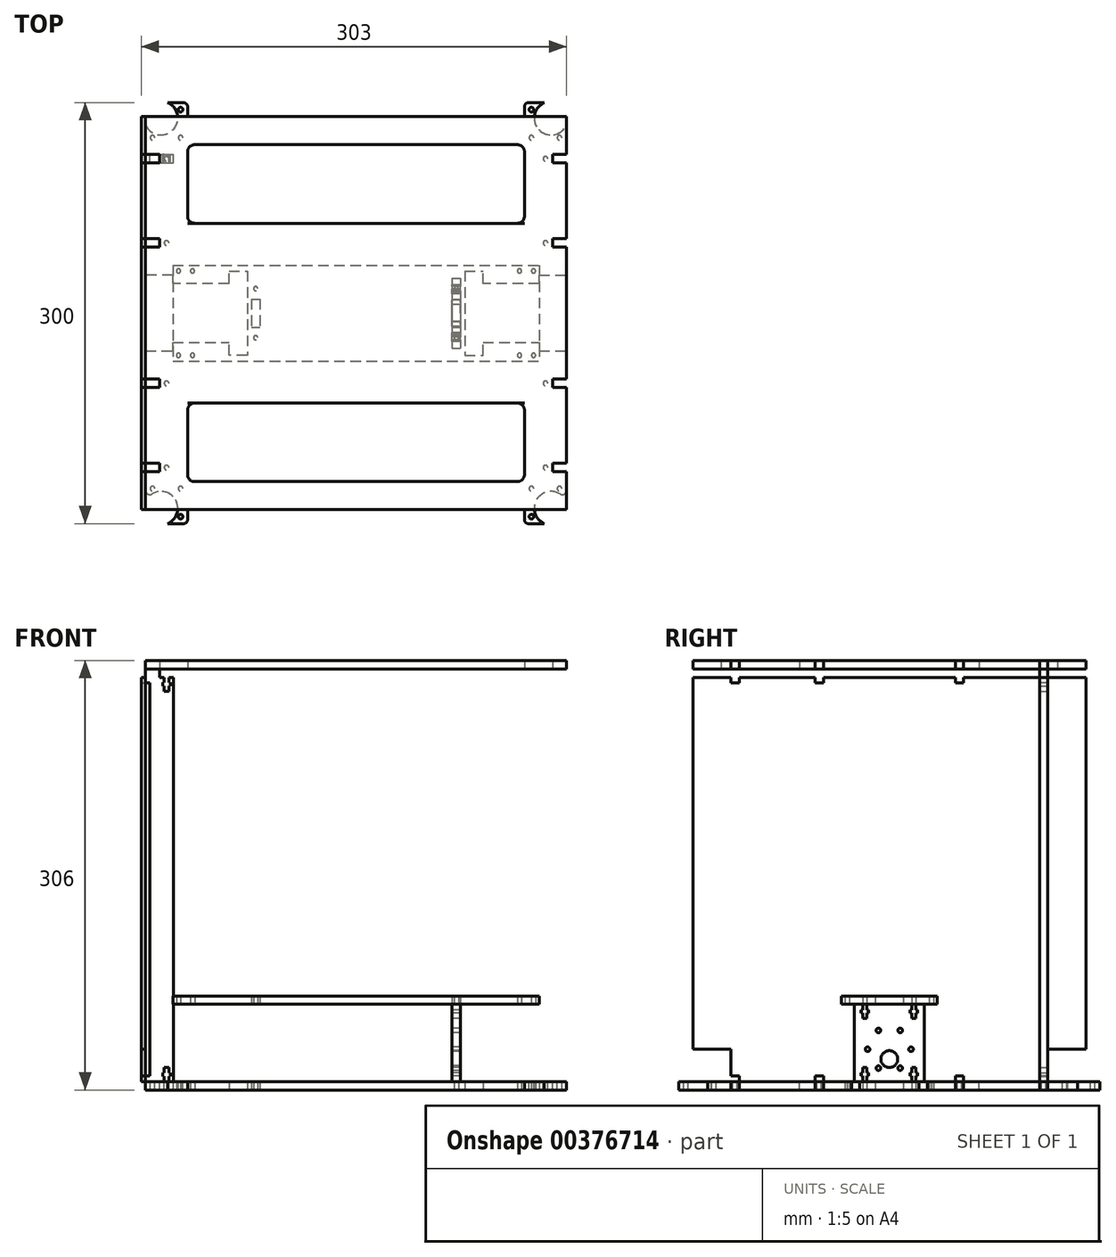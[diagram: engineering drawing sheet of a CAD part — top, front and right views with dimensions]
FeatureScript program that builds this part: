
annotation { "Feature Type Name" : "Feature", "Feature Type Description" : "" }
export const myFeature = defineFeature(function(context is Context, id is Id, definition is map)
    precondition{}
    {
        {
            var Q0;
            Q0=qCreatedBy(makeId("Top.planeOp"),FACE);
            var sketch = newSketch(context, id + "F0", { "sketchPlane" : qUnion([Q0])});
            skLineSegment(sketch, "E0.bottom", {"start": v(150, 34.05) * mm, "end": v(-150, 34.05) * mm});
            skLineSegment(sketch, "E0.top", {"start": v(150, -34.05) * mm, "end": v(-150, -34.05) * mm});
            skLineSegment(sketch, "E0.left", {"start": v(150, 34.05) * mm, "end": v(150, 27) * mm});
            skLineSegment(sketch, "E0.right", {"start": v(-150, 34.05) * mm, "end": v(-150, 27) * mm});
            skPoint(sketch, "E0.middle", {"position": v(0, 0) * mm});
            skPoint(sketch, "E1", {"position": v(126.5, -30.05) * mm});
            skPoint(sketch, "E2", {"position": v(116.5, -30.05) * mm});
            skPoint(sketch, "E3", {"position": v(126.5, 30.05) * mm});
            skPoint(sketch, "E4", {"position": v(116.5, 30.05) * mm});
            skPoint(sketch, "E5", {"position": v(-116.5, -30.05) * mm});
            skPoint(sketch, "E6", {"position": v(-126.5, -30.05) * mm});
            skPoint(sketch, "E7", {"position": v(-126.5, 30.05) * mm});
            skPoint(sketch, "E8", {"position": v(-116.5, 30.05) * mm});
            skLineSegment(sketch, "E9", {"start": v(130.5, 21) * mm, "end": v(90.5, 21) * mm});
            skLineSegment(sketch, "E10", {"start": v(90.5, 21) * mm, "end": v(90.5, -21) * mm, "construction": true});
            skLineSegment(sketch, "E11", {"start": v(90.5, -21) * mm, "end": v(130.5, -21) * mm});
            skLineSegment(sketch, "E12", {"start": v(130.5, -21) * mm, "end": v(130.5, -27) * mm});
            skLineSegment(sketch, "E13", {"start": v(130.5, -27) * mm, "end": v(150, -27) * mm});
            skLineSegment(sketch, "E14", {"start": v(130.5, 21) * mm, "end": v(130.5, 27) * mm});
            skLineSegment(sketch, "E15", {"start": v(130.5, 27) * mm, "end": v(150, 27) * mm});
            skLineSegment(sketch, "E16.trimOffspring", {"start": v(150, -27) * mm, "end": v(150, -34.05) * mm});
            skPoint(sketch, "E17", {"position": v(90.5, 0) * mm});
            skLineSegment(sketch, "E18", {"start": v(-150, -27) * mm, "end": v(-130.5, -27) * mm});
            skLineSegment(sketch, "E19", {"start": v(-130.5, -27) * mm, "end": v(-130.5, -21) * mm});
            skLineSegment(sketch, "E20", {"start": v(-130.5, -21) * mm, "end": v(-90.5, -21) * mm});
            skLineSegment(sketch, "E21", {"start": v(-90.5, 21) * mm, "end": v(-130.5, 21) * mm});
            skLineSegment(sketch, "E22", {"start": v(-130.5, 21) * mm, "end": v(-130.5, 27) * mm});
            skLineSegment(sketch, "E23", {"start": v(-130.5, 27) * mm, "end": v(-150, 27) * mm});
            skLineSegment(sketch, "E24.trimOffspring", {"start": v(-150, -27) * mm, "end": v(-150, -34.05) * mm});
            skLineSegment(sketch, "E25", {"start": v(68.5, 25) * mm, "end": v(68.5, -25) * mm, "construction": true});
            skPoint(sketch, "E26", {"position": v(68.5, 0) * mm});
            skLineSegment(sketch, "E27.bottom", {"start": v(74.5, 10) * mm, "end": v(68.5, 10) * mm});
            skLineSegment(sketch, "E27.top", {"start": v(74.5, -10) * mm, "end": v(68.5, -10) * mm});
            skLineSegment(sketch, "E27.left", {"start": v(74.5, 10) * mm, "end": v(74.5, -10) * mm});
            skLineSegment(sketch, "E27.right", {"start": v(68.5, 10) * mm, "end": v(68.5, -10) * mm});
            skCircle(sketch, "E28", {"center": v(71.5, 17.5) * mm, "radius": 1.5 * mm});
            skCircle(sketch, "E29", {"center": v(71.5, -17.5) * mm, "radius": 1.5 * mm});
            skLineSegment(sketch, "E30", {"start": v(71.5, 17.5) * mm, "end": v(71.5, -17.5) * mm, "construction": true});
            skPoint(sketch, "E31", {"position": v(71.5, 0) * mm});
            skLineSegment(sketch, "E32", {"start": v(68.5, 0) * mm, "end": v(74.5, 0) * mm, "construction": true});
            skLineSegment(sketch, "E33.bottom", {"start": v(-74.5, 10) * mm, "end": v(-68.5, 10) * mm});
            skLineSegment(sketch, "E33.top", {"start": v(-74.5, -10) * mm, "end": v(-68.5, -10) * mm});
            skLineSegment(sketch, "E33.left", {"start": v(-74.5, 10) * mm, "end": v(-74.5, -10) * mm});
            skLineSegment(sketch, "E33.right", {"start": v(-68.5, 10) * mm, "end": v(-68.5, -10) * mm});
            skCircle(sketch, "E34", {"center": v(-71.5, 17.5) * mm, "radius": 1.5 * mm});
            skCircle(sketch, "E35", {"center": v(-71.5, -17.5) * mm, "radius": 1.5 * mm});
            skLineSegment(sketch, "E36.bottom", {"start": v(77.5, 30) * mm, "end": v(90.5, 30) * mm});
            skLineSegment(sketch, "E36.top", {"start": v(77.5, -30) * mm, "end": v(90.5, -30) * mm});
            skLineSegment(sketch, "E36.left", {"start": v(77.5, 30) * mm, "end": v(77.5, -30) * mm});
            skLineSegment(sketch, "E37", {"start": v(90.5, -30) * mm, "end": v(90.5, -21) * mm});
            skLineSegment(sketch, "E38", {"start": v(90.5, 21) * mm, "end": v(90.5, 30) * mm});
            skLineSegment(sketch, "E39", {"start": v(-90.5, 21) * mm, "end": v(-90.5, 30) * mm});
            skLineSegment(sketch, "E40", {"start": v(-90.5, 30) * mm, "end": v(-77.5, 30) * mm});
            skLineSegment(sketch, "E41", {"start": v(-77.5, 30) * mm, "end": v(-77.5, -30) * mm});
            skLineSegment(sketch, "E42", {"start": v(-77.5, -30) * mm, "end": v(-90.5, -30) * mm});
            skLineSegment(sketch, "E43", {"start": v(-90.5, -30) * mm, "end": v(-90.5, -21) * mm});
            skSolve(sketch);
        }
        {
            var Q0;
            Q0=qSketchRegion(id+"F0",true);
            extrude(context, id + "F1", {"entities" : qUnion([Q0]), "depth" : 6 * mm});
        }
        {
            var Q0;
            Q0=sQuery(id+"F0.wireOp",VERTEX,"E1");
            var Q1;
            Q1=sQuery(id+"F0.wireOp",VERTEX,"E2");
            var Q2;
            Q2=sQuery(id+"F0.wireOp",VERTEX,"E3");
            var Q3;
            Q3=sQuery(id+"F0.wireOp",VERTEX,"E4");
            var Q4;
            Q4=sQuery(id+"F0.wireOp",VERTEX,"E5");
            var Q5;
            Q5=sQuery(id+"F0.wireOp",VERTEX,"E6");
            var Q6;
            Q6=sQuery(id+"F0.wireOp",VERTEX,"E8");
            var Q7;
            Q7=sQuery(id+"F0.wireOp",VERTEX,"E7");
            var Q8;
            Q8=makeQuery(id+"F1.opExtrude","SWEPT_BODY",BODY,{"disambiguationData":[OSD([sQuery(id+"F0.wireOp",EDGE,"E0.bottom"),sQuery(id+"F0.wireOp",EDGE,"E0.top"),sQuery(id+"F0.wireOp",EDGE,"E0.left"),sQuery(id+"F0.wireOp",EDGE,"E0.right")])]});
            hole(context, id + "F2", {"style" : HoleStyle.SIMPLE, "endStyle" : HoleEndStyle.THROUGH, "oppositeDirection" : true, "standardTappedOrClearance" : lookupTablePath({ "standard" : "ISO", "size" : "3", "type" : "Drilled" }), "standardBlindInLast" : lookupTablePath({ "standard" : "ISO", "size" : "3", "type" : "Drilled" }), "holeDiameter" : 3 * mm, "tappedDepth" : 10.9 * mm, "tapClearance" : 3, "locations" : qUnion([Q0, Q1, Q2, Q3, Q4, Q5, Q6, Q7]), "scope" : qUnion([Q8])});
        }
        {
            var Q0;
            Q0=makeQuery(id+"F1.opExtrude","CAP_FACE",FACE,{"disambiguationData":[OSD([sQuery(id+"F0.wireOp",EDGE,"E0.bottom"),sQuery(id+"F0.wireOp",EDGE,"E0.top"),sQuery(id+"F0.wireOp",EDGE,"E0.left"),sQuery(id+"F0.wireOp",EDGE,"E0.right"),sQuery(id+"F0.wireOp",EDGE,"E9"),sQuery(id+"F0.wireOp",EDGE,"E10"),sQuery(id+"F0.wireOp",EDGE,"E11"),sQuery(id+"F0.wireOp",EDGE,"E12"),sQuery(id+"F0.wireOp",EDGE,"E13"),sQuery(id+"F0.wireOp",EDGE,"E14"),sQuery(id+"F0.wireOp",EDGE,"E15"),sQuery(id+"F0.wireOp",EDGE,"E16.trimOffspring"),sQuery(id+"F0.wireOp",EDGE,"E18"),sQuery(id+"F0.wireOp",EDGE,"E19"),sQuery(id+"F0.wireOp",EDGE,"E20"),sQuery(id+"F0.wireOp",EDGE,"jEcUEht7-0Wzt-mQMa-QwQx-0Txn2W36VDiV"),sQuery(id+"F0.wireOp",EDGE,"E21"),sQuery(id+"F0.wireOp",EDGE,"E22"),sQuery(id+"F0.wireOp",EDGE,"E23"),sQuery(id+"F0.wireOp",EDGE,"E24.trimOffspring")])],"isStart":false});
            var sketch = newSketch(context, id + "F3", { "sketchPlane" : qUnion([Q0])});
            skLineSegment(sketch, "E44.bottom", {"start": v(68.5, 25) * mm, "end": v(74.5, 25) * mm});
            skLineSegment(sketch, "E44.top", {"start": v(68.5, -25) * mm, "end": v(74.5, -25) * mm});
            skLineSegment(sketch, "E44.left", {"start": v(68.5, 25) * mm, "end": v(68.5, -25) * mm});
            skLineSegment(sketch, "E44.right", {"start": v(74.5, 25) * mm, "end": v(74.5, -25) * mm});
            skSolve(sketch);
        }
        {
            var Q0;
            Q0=qSketchRegion(id+"F3",true);
            extrude(context, id + "F4", {"entities" : qUnion([Q0]), "depth" : 55 * mm});
        }
        {
            var Q0;
            Q0=makeQuery(id+"F4.opExtrude","CAP_FACE",FACE,{"disambiguationData":[OSD([sQuery(id+"F3.wireOp",EDGE,"E44.bottom"),sQuery(id+"F3.wireOp",EDGE,"E44.top"),sQuery(id+"F3.wireOp",EDGE,"E44.left"),sQuery(id+"F3.wireOp",EDGE,"E44.right")])],"isStart":true});
            var sketch = newSketch(context, id + "F5", { "sketchPlane" : qUnion([Q0])});
            skLineSegment(sketch, "E45.bottom", {"start": v(74.5, -10) * mm, "end": v(68.5, -10) * mm});
            skLineSegment(sketch, "E45.top", {"start": v(74.5, 10) * mm, "end": v(68.5, 10) * mm});
            skLineSegment(sketch, "E45.left", {"start": v(74.5, -10) * mm, "end": v(74.5, 10) * mm});
            skLineSegment(sketch, "E45.right", {"start": v(68.5, -10) * mm, "end": v(68.5, 10) * mm});
            skSolve(sketch);
        }
        {
            var Q0;
            Q0=qSketchRegion(id+"F5",true);
            extrude(context, id + "F6", {"entities" : qUnion([Q0]), "operationType" : NewBodyOperationType.ADD, "depth" : 6 * mm});
        }
        {
            var Q0;
            Q0=makeQuery(id+"F4.opExtrude","SWEPT_FACE",FACE,{"disambiguationData":[OSD([sQuery(id+"F3.wireOp",EDGE,"E44.left")])]});
            var sketch = newSketch(context, id + "F7", { "sketchPlane" : qUnion([Q0])});
            skCircle(sketch, "E46", {"center": v(0, 29) * mm, "radius": 15.5 * mm, "construction": true});
            skCircle(sketch, "E47", {"center": v(0, 22) * mm, "radius": 6 * mm});
            skCircle(sketch, "E48", {"center": v(7.75, 15.58) * mm, "radius": 1.65 * mm});
            skCircle(sketch, "E49", {"center": v(15.5, 29) * mm, "radius": 1.65 * mm});
            skCircle(sketch, "E50", {"center": v(7.75, 42.42) * mm, "radius": 1.65 * mm});
            skCircle(sketch, "E51", {"center": v(-7.75, 42.42) * mm, "radius": 1.65 * mm});
            skCircle(sketch, "E52", {"center": v(-15.5, 29) * mm, "radius": 1.65 * mm});
            skCircle(sketch, "E53", {"center": v(-7.75, 15.58) * mm, "radius": 1.65 * mm});
            skLineSegment(sketch, "E54", {"start": v(-7.75, 15.58) * mm, "end": v(0, 29) * mm, "construction": true});
            skLineSegment(sketch, "E55", {"start": v(7.75, 15.58) * mm, "end": v(0, 29) * mm, "construction": true});
            skLineSegment(sketch, "E56", {"start": v(0, 29) * mm, "end": v(15.5, 29) * mm, "construction": true});
            skLineSegment(sketch, "E57", {"start": v(0, 29) * mm, "end": v(7.75, 42.42) * mm, "construction": true});
            skLineSegment(sketch, "E58", {"start": v(0, 29) * mm, "end": v(-7.75, 42.42) * mm, "construction": true});
            skLineSegment(sketch, "E59", {"start": v(0, 29) * mm, "end": v(-15.5, 29) * mm, "construction": true});
            skSolve(sketch);
        }
        {
            var Q0;
            Q0=qSketchRegion(id+"F7",true);
            extrude(context, id + "F8", {"entities" : qUnion([Q0]), "operationType" : NewBodyOperationType.REMOVE, "endBound" : BoundingType.UP_TO_NEXT, "oppositeDirection" : true, "depth" : 25 * mm});
        }
        {
            var Q0;
            Q0=makeQuery(id+"F6.boolean.opBoolean","MERGE",FACE,{"derivedFrom":[makeQuery(id+"F4.opExtrude","SWEPT_FACE",FACE,{"disambiguationData":[OSD([sQuery(id+"F3.wireOp",EDGE,"E44.left")])]}),makeQuery(id+"F6.opExtrude","SWEPT_FACE",FACE,{"disambiguationData":[OSD([sQuery(id+"F5.wireOp",EDGE,"E45.right")])]})]});
            var sketch = newSketch(context, id + "F9", { "sketchPlane" : qUnion([Q0])});
            skLineSegment(sketch, "E60", {"start": v(19, 6) * mm, "end": v(19, 10) * mm});
            skLineSegment(sketch, "E61", {"start": v(19, 10) * mm, "end": v(20.2, 10) * mm});
            skLineSegment(sketch, "E62", {"start": v(20.2, 10) * mm, "end": v(20.2, 12.3) * mm});
            skLineSegment(sketch, "E63", {"start": v(20.2, 12.3) * mm, "end": v(19, 12.3) * mm});
            skLineSegment(sketch, "E64", {"start": v(19, 12.3) * mm, "end": v(19, 16) * mm});
            skLineSegment(sketch, "E65", {"start": v(19, 16) * mm, "end": v(16, 16) * mm});
            skLineSegment(sketch, "E66", {"start": v(16, 16) * mm, "end": v(16, 12.3) * mm});
            skLineSegment(sketch, "E67", {"start": v(16, 12.3) * mm, "end": v(14.8, 12.3) * mm});
            skLineSegment(sketch, "E68", {"start": v(14.8, 12.3) * mm, "end": v(14.8, 10) * mm});
            skLineSegment(sketch, "E69", {"start": v(14.8, 10) * mm, "end": v(16, 10) * mm});
            skLineSegment(sketch, "E70", {"start": v(16, 10) * mm, "end": v(16, 6) * mm});
            skLineSegment(sketch, "E71", {"start": v(16, 6) * mm, "end": v(19, 6) * mm});
            skPoint(sketch, "E72", {"position": v(17.5, 16) * mm});
            skLineSegment(sketch, "E73", {"start": v(-19, 6) * mm, "end": v(-19, 10) * mm});
            skLineSegment(sketch, "E74", {"start": v(-19, 10) * mm, "end": v(-20.2, 10) * mm});
            skLineSegment(sketch, "E75", {"start": v(-20.2, 10) * mm, "end": v(-20.2, 12.3) * mm});
            skLineSegment(sketch, "E76", {"start": v(-20.2, 12.3) * mm, "end": v(-19, 12.3) * mm});
            skLineSegment(sketch, "E77", {"start": v(-19, 12.3) * mm, "end": v(-19, 16) * mm});
            skLineSegment(sketch, "E78", {"start": v(-19, 16) * mm, "end": v(-16, 16) * mm});
            skLineSegment(sketch, "E79", {"start": v(-16, 16) * mm, "end": v(-16, 12.3) * mm});
            skLineSegment(sketch, "E80", {"start": v(-16, 12.3) * mm, "end": v(-14.8, 12.3) * mm});
            skLineSegment(sketch, "E81", {"start": v(-14.8, 12.3) * mm, "end": v(-14.8, 10) * mm});
            skLineSegment(sketch, "E82", {"start": v(-14.8, 10) * mm, "end": v(-16, 10) * mm});
            skLineSegment(sketch, "E83", {"start": v(-16, 10) * mm, "end": v(-16, 6) * mm});
            skLineSegment(sketch, "E84", {"start": v(-16, 6) * mm, "end": v(-19, 6) * mm});
            skLineSegment(sketch, "E85", {"start": v(25, 33.5) * mm, "end": v(-25, 33.5) * mm, "construction": true});
            skLineSegment(sketch, "E86", {"start": v(16, 61) * mm, "end": v(19, 61) * mm});
            skLineSegment(sketch, "E87", {"start": v(19, 61) * mm, "end": v(19, 57) * mm});
            skLineSegment(sketch, "E88", {"start": v(19, 57) * mm, "end": v(20.2, 57) * mm});
            skLineSegment(sketch, "E89", {"start": v(20.2, 57) * mm, "end": v(20.2, 54.7) * mm});
            skLineSegment(sketch, "E90", {"start": v(20.2, 54.7) * mm, "end": v(19, 54.7) * mm});
            skLineSegment(sketch, "E91", {"start": v(19, 54.7) * mm, "end": v(19, 51) * mm});
            skLineSegment(sketch, "E92", {"start": v(19, 51) * mm, "end": v(16, 51) * mm});
            skLineSegment(sketch, "E93", {"start": v(16, 51) * mm, "end": v(16, 54.7) * mm});
            skLineSegment(sketch, "E94", {"start": v(16, 54.7) * mm, "end": v(14.8, 54.7) * mm});
            skLineSegment(sketch, "E95", {"start": v(14.8, 54.7) * mm, "end": v(14.8, 57) * mm});
            skLineSegment(sketch, "E96", {"start": v(14.8, 57) * mm, "end": v(16, 57) * mm});
            skLineSegment(sketch, "E97", {"start": v(16, 57) * mm, "end": v(16, 61) * mm});
            skLineSegment(sketch, "E98", {"start": v(-19, 61) * mm, "end": v(-16, 61) * mm});
            skLineSegment(sketch, "E99", {"start": v(-16, 61) * mm, "end": v(-16, 57) * mm});
            skLineSegment(sketch, "E100", {"start": v(-16, 57) * mm, "end": v(-14.8, 57) * mm});
            skLineSegment(sketch, "E101", {"start": v(-14.8, 57) * mm, "end": v(-14.8, 54.7) * mm});
            skLineSegment(sketch, "E102", {"start": v(-14.8, 54.7) * mm, "end": v(-16, 54.7) * mm});
            skLineSegment(sketch, "E103", {"start": v(-16, 54.7) * mm, "end": v(-16, 51) * mm});
            skLineSegment(sketch, "E104", {"start": v(-16, 51) * mm, "end": v(-19, 51) * mm});
            skLineSegment(sketch, "E105", {"start": v(-19, 51) * mm, "end": v(-19, 54.7) * mm});
            skLineSegment(sketch, "E106", {"start": v(-19, 54.7) * mm, "end": v(-20.2, 54.7) * mm});
            skLineSegment(sketch, "E107", {"start": v(-20.2, 54.7) * mm, "end": v(-20.2, 57) * mm});
            skLineSegment(sketch, "E108", {"start": v(-20.2, 57) * mm, "end": v(-19, 57) * mm});
            skLineSegment(sketch, "E109", {"start": v(-19, 57) * mm, "end": v(-19, 61) * mm});
            skSolve(sketch);
        }
        {
            var Q0;
            Q0=qSketchRegion(id+"F9",true);
            extrude(context, id + "F10", {"entities" : qUnion([Q0]), "operationType" : NewBodyOperationType.REMOVE, "endBound" : BoundingType.UP_TO_NEXT, "oppositeDirection" : true, "depth" : 25 * mm});
        }
        {
            var Q0;
            {var subQ0=sQuery(id+"F3.wireOp",EDGE,"E44.right");var subQ1=sQuery(id+"F3.wireOp",EDGE,"E44.left");Q0=makeQuery(id+"F10.boolean.opBoolean","SPLIT",FACE,{"disambiguationData":[TD([makeQuery(id+"F10.opExtrude","SWEPT_FACE",FACE,{"disambiguationData":[OSD([sQuery(id+"F9.wireOp",EDGE,"E97")])]})])],"derivedFrom":makeQuery(id+"F4.opExtrude","CAP_FACE",FACE,{"disambiguationData":[OSD([sQuery(id+"F3.wireOp",EDGE,"E44.bottom"),sQuery(id+"F3.wireOp",EDGE,"E44.top"),subQ1,subQ0])],"isStart":false})});}
            var sketch = newSketch(context, id + "F11", { "sketchPlane" : qUnion([Q0])});
            skLineSegment(sketch, "E110.bottom", {"start": v(68.5, 10) * mm, "end": v(74.5, 10) * mm});
            skLineSegment(sketch, "E110.top", {"start": v(68.5, -10) * mm, "end": v(74.5, -10) * mm});
            skLineSegment(sketch, "E110.left", {"start": v(68.5, 10) * mm, "end": v(68.5, -10) * mm});
            skLineSegment(sketch, "E110.right", {"start": v(74.5, 10) * mm, "end": v(74.5, -10) * mm});
            skSolve(sketch);
        }
        {
            var Q0;
            Q0=qSketchRegion(id+"F11",true);
            extrude(context, id + "F12", {"entities" : qUnion([Q0]), "operationType" : NewBodyOperationType.ADD, "depth" : 6 * mm});
        }
        {
            var Q0;
            {var subQ2=sQuery(id+"F3.wireOp",EDGE,"E44.right");var subQ4=sQuery(id+"F3.wireOp",EDGE,"E44.left");var subQ6=makeQuery(id+"F10.opExtrude","SWEPT_FACE",FACE,{"disambiguationData":[OSD([sQuery(id+"F9.wireOp",EDGE,"E99")])]});Q0=makeQuery(id+"F12.boolean.opBoolean","SPLIT",FACE,{"disambiguationData":[TD([makeQuery(id+"F10.boolean.opBoolean","COPY",FACE,{"derivedFrom":subQ6})])],"derivedFrom":makeQuery(id+"F10.boolean.opBoolean","SPLIT",FACE,{"disambiguationData":[TD([makeQuery(id+"F10.opExtrude","SWEPT_FACE",FACE,{"disambiguationData":[OSD([sQuery(id+"F9.wireOp",EDGE,"E97")])]})])],"derivedFrom":makeQuery(id+"F4.opExtrude","CAP_FACE",FACE,{"disambiguationData":[OSD([sQuery(id+"F3.wireOp",EDGE,"E44.bottom"),sQuery(id+"F3.wireOp",EDGE,"E44.top"),subQ4,subQ2])],"isStart":false})})});}
            var sketch = newSketch(context, id + "F13", { "sketchPlane" : qUnion([Q0])});
            skLineSegment(sketch, "E111.bottom", {"start": v(-130.5, 34.05) * mm, "end": v(130.5, 34.05) * mm});
            skLineSegment(sketch, "E111.top", {"start": v(-130.5, -34.05) * mm, "end": v(130.5, -34.05) * mm});
            skLineSegment(sketch, "E111.left", {"start": v(-130.5, 34.05) * mm, "end": v(-130.5, -34.05) * mm});
            skLineSegment(sketch, "E111.right", {"start": v(130.5, 34.05) * mm, "end": v(130.5, -34.05) * mm});
            skLineSegment(sketch, "E112.bottom", {"start": v(68.5, 10) * mm, "end": v(74.5, 10) * mm});
            skLineSegment(sketch, "E112.top", {"start": v(68.5, -10) * mm, "end": v(74.5, -10) * mm});
            skLineSegment(sketch, "E112.left", {"start": v(68.5, 10) * mm, "end": v(68.5, -10) * mm});
            skLineSegment(sketch, "E112.right", {"start": v(74.5, 10) * mm, "end": v(74.5, -10) * mm});
            skLineSegment(sketch, "E113", {"start": v(0, 34.05) * mm, "end": v(0, -34.05) * mm, "construction": true});
            skLineSegment(sketch, "E114.bottom", {"start": v(-74.5, 10) * mm, "end": v(-68.5, 10) * mm});
            skLineSegment(sketch, "E114.top", {"start": v(-74.5, -10) * mm, "end": v(-68.5, -10) * mm});
            skLineSegment(sketch, "E114.left", {"start": v(-74.5, 10) * mm, "end": v(-74.5, -10) * mm});
            skLineSegment(sketch, "E114.right", {"start": v(-68.5, 10) * mm, "end": v(-68.5, -10) * mm});
            skCircle(sketch, "E115", {"center": v(-71.5, 17.5) * mm, "radius": 1.5 * mm});
            skCircle(sketch, "E116", {"center": v(-71.5, -17.5) * mm, "radius": 1.5 * mm});
            skCircle(sketch, "E117", {"center": v(-126.5, 30.05) * mm, "radius": 1.5 * mm});
            skCircle(sketch, "E118", {"center": v(-116.5, 30.05) * mm, "radius": 1.5 * mm});
            skCircle(sketch, "E119", {"center": v(-126.5, -30.05) * mm, "radius": 1.5 * mm});
            skCircle(sketch, "E120", {"center": v(-116.5, -30.05) * mm, "radius": 1.5 * mm});
            skCircle(sketch, "E121", {"center": v(116.5, -30.05) * mm, "radius": 1.5 * mm});
            skCircle(sketch, "E122", {"center": v(126.5, -30.05) * mm, "radius": 1.5 * mm});
            skCircle(sketch, "E123", {"center": v(116.5, 30.05) * mm, "radius": 1.5 * mm});
            skCircle(sketch, "E124", {"center": v(126.5, 30.05) * mm, "radius": 1.5 * mm});
            skCircle(sketch, "E125", {"center": v(71.5, -17.5) * mm, "radius": 1.5 * mm});
            skCircle(sketch, "E126", {"center": v(71.5, 17.5) * mm, "radius": 1.5 * mm});
            skSolve(sketch);
        }
        {
            var Q0;
            Q0=qSketchRegion(id+"F13",true);
            extrude(context, id + "F14", {"entities" : qUnion([Q0]), "depth" : 6 * mm});
        }
        {
            var Q0;
            Q0=makeQuery(id+"F1.opExtrude","CAP_FACE",FACE,{"disambiguationData":[OSD([sQuery(id+"F0.wireOp",EDGE,"E0.bottom"),sQuery(id+"F0.wireOp",EDGE,"E0.top"),sQuery(id+"F0.wireOp",EDGE,"E0.left"),sQuery(id+"F0.wireOp",EDGE,"E0.right"),sQuery(id+"F0.wireOp",EDGE,"E9"),sQuery(id+"F0.wireOp",EDGE,"E11"),sQuery(id+"F0.wireOp",EDGE,"E12"),sQuery(id+"F0.wireOp",EDGE,"E13"),sQuery(id+"F0.wireOp",EDGE,"E14"),sQuery(id+"F0.wireOp",EDGE,"E15"),sQuery(id+"F0.wireOp",EDGE,"E16.trimOffspring"),sQuery(id+"F0.wireOp",EDGE,"E18"),sQuery(id+"F0.wireOp",EDGE,"E19"),sQuery(id+"F0.wireOp",EDGE,"E20"),sQuery(id+"F0.wireOp",EDGE,"E21"),sQuery(id+"F0.wireOp",EDGE,"E22"),sQuery(id+"F0.wireOp",EDGE,"E23"),sQuery(id+"F0.wireOp",EDGE,"E24.trimOffspring"),sQuery(id+"F0.wireOp",EDGE,"E27.bottom"),sQuery(id+"F0.wireOp",EDGE,"E27.top"),sQuery(id+"F0.wireOp",EDGE,"E27.left"),sQuery(id+"F0.wireOp",EDGE,"E27.right"),sQuery(id+"F0.wireOp",EDGE,"E28"),sQuery(id+"F0.wireOp",EDGE,"E29"),sQuery(id+"F0.wireOp",EDGE,"E33.bottom"),sQuery(id+"F0.wireOp",EDGE,"E33.top"),sQuery(id+"F0.wireOp",EDGE,"E33.left"),sQuery(id+"F0.wireOp",EDGE,"E33.right"),sQuery(id+"F0.wireOp",EDGE,"E34"),sQuery(id+"F0.wireOp",EDGE,"E35"),sQuery(id+"F0.wireOp",EDGE,"E36.bottom"),sQuery(id+"F0.wireOp",EDGE,"E36.top"),sQuery(id+"F0.wireOp",EDGE,"E36.left"),sQuery(id+"F0.wireOp",EDGE,"E37"),sQuery(id+"F0.wireOp",EDGE,"E38"),sQuery(id+"F0.wireOp",EDGE,"E39"),sQuery(id+"F0.wireOp",EDGE,"E40"),sQuery(id+"F0.wireOp",EDGE,"E41"),sQuery(id+"F0.wireOp",EDGE,"E42"),sQuery(id+"F0.wireOp",EDGE,"E43")])],"isStart":false});
            var sketch = newSketch(context, id + "F15", { "sketchPlane" : qUnion([Q0])});
            skLineSegment(sketch, "E127", {"start": v(0, 34.05) * mm, "end": v(0, -34.05) * mm, "construction": true});
            skLineSegment(sketch, "E128", {"start": v(-77.5, 0) * mm, "end": v(77.5, 0) * mm, "construction": true});
            skLineSegment(sketch, "E129", {"start": v(-150, 34.05) * mm, "end": v(-150, 150) * mm});
            skLineSegment(sketch, "E130", {"start": v(-150, 150) * mm, "end": v(-120, 150) * mm});
            skLineSegment(sketch, "E131", {"start": v(-120, 150) * mm, "end": v(-120, 64.05) * mm});
            skLineSegment(sketch, "E132", {"start": v(-120, 64.05) * mm, "end": v(0, 64.05) * mm});
            skLineSegment(sketch, "E133.MirrorCS", {"start": v(150, 34.05) * mm, "end": v(150, 150) * mm});
            skLineSegment(sketch, "E134.MirrorCS", {"start": v(150, 150) * mm, "end": v(120, 150) * mm});
            skLineSegment(sketch, "E135.MirrorCS", {"start": v(120, 150) * mm, "end": v(120, 64.05) * mm});
            skLineSegment(sketch, "E136.MirrorCS", {"start": v(120, 64.05) * mm, "end": v(0, 64.05) * mm});
            skLineSegment(sketch, "E137.MirrorCS", {"start": v(-150, -34.05) * mm, "end": v(-150, -150) * mm});
            skLineSegment(sketch, "E138.MirrorCS", {"start": v(150, -34.05) * mm, "end": v(150, -150) * mm});
            skLineSegment(sketch, "E139.MirrorCS", {"start": v(120, -150) * mm, "end": v(120, -64.05) * mm});
            skLineSegment(sketch, "E140.MirrorCS", {"start": v(120, -64.05) * mm, "end": v(0, -64.05) * mm});
            skLineSegment(sketch, "E141.MirrorCS", {"start": v(150, -150) * mm, "end": v(120, -150) * mm});
            skLineSegment(sketch, "E142.MirrorCS", {"start": v(-120, -64.05) * mm, "end": v(0, -64.05) * mm});
            skLineSegment(sketch, "E143.MirrorCS", {"start": v(-150, -150) * mm, "end": v(-120, -150) * mm});
            skLineSegment(sketch, "E144.MirrorCS", {"start": v(-120, -150) * mm, "end": v(-120, -64.05) * mm});
            skLineSegment(sketch, "E145", {"start": v(-150, 34.05) * mm, "end": v(0, 34.05) * mm});
            skLineSegment(sketch, "E146.MirrorCS", {"start": v(150, 34.05) * mm, "end": v(0, 34.05) * mm});
            skLineSegment(sketch, "E147.MirrorCS", {"start": v(150, -34.05) * mm, "end": v(0, -34.05) * mm});
            skLineSegment(sketch, "E148.MirrorCS", {"start": v(-150, -34.05) * mm, "end": v(0, -34.05) * mm});
            skSolve(sketch);
        }
        {
            var Q0;
            Q0 = qSketchRegion(id + "F15", true);
            extrude(context, id + "F16", {"entities" : qUnion([Q0]), "operationType" : NewBodyOperationType.ADD, "oppositeDirection" : true, "depth" : 6 * mm});
        }
        {
            var Q0;
            Q0=makeQuery(id+"F16.boolean.opBoolean","MERGE",FACE,{"derivedFrom":[makeQuery(id+"F1.opExtrude","CAP_FACE",FACE,{"disambiguationData":[OSD([sQuery(id+"F0.wireOp",EDGE,"E0.bottom"),sQuery(id+"F0.wireOp",EDGE,"E0.top"),sQuery(id+"F0.wireOp",EDGE,"E0.left"),sQuery(id+"F0.wireOp",EDGE,"E0.right"),sQuery(id+"F0.wireOp",EDGE,"E9"),sQuery(id+"F0.wireOp",EDGE,"E11"),sQuery(id+"F0.wireOp",EDGE,"E12"),sQuery(id+"F0.wireOp",EDGE,"E13"),sQuery(id+"F0.wireOp",EDGE,"E14"),sQuery(id+"F0.wireOp",EDGE,"E15"),sQuery(id+"F0.wireOp",EDGE,"E16.trimOffspring"),sQuery(id+"F0.wireOp",EDGE,"E18"),sQuery(id+"F0.wireOp",EDGE,"E19"),sQuery(id+"F0.wireOp",EDGE,"E20"),sQuery(id+"F0.wireOp",EDGE,"E21"),sQuery(id+"F0.wireOp",EDGE,"E22"),sQuery(id+"F0.wireOp",EDGE,"E23"),sQuery(id+"F0.wireOp",EDGE,"E24.trimOffspring"),sQuery(id+"F0.wireOp",EDGE,"E27.bottom"),sQuery(id+"F0.wireOp",EDGE,"E27.top"),sQuery(id+"F0.wireOp",EDGE,"E27.left"),sQuery(id+"F0.wireOp",EDGE,"E27.right"),sQuery(id+"F0.wireOp",EDGE,"E28"),sQuery(id+"F0.wireOp",EDGE,"E29"),sQuery(id+"F0.wireOp",EDGE,"E33.bottom"),sQuery(id+"F0.wireOp",EDGE,"E33.top"),sQuery(id+"F0.wireOp",EDGE,"E33.left"),sQuery(id+"F0.wireOp",EDGE,"E33.right"),sQuery(id+"F0.wireOp",EDGE,"E34"),sQuery(id+"F0.wireOp",EDGE,"E35"),sQuery(id+"F0.wireOp",EDGE,"E36.bottom"),sQuery(id+"F0.wireOp",EDGE,"E36.top"),sQuery(id+"F0.wireOp",EDGE,"E36.left"),sQuery(id+"F0.wireOp",EDGE,"E37"),sQuery(id+"F0.wireOp",EDGE,"E38"),sQuery(id+"F0.wireOp",EDGE,"E39"),sQuery(id+"F0.wireOp",EDGE,"E40"),sQuery(id+"F0.wireOp",EDGE,"E41"),sQuery(id+"F0.wireOp",EDGE,"E42"),sQuery(id+"F0.wireOp",EDGE,"E43")])],"isStart":false}),makeQuery(id+"F16.opExtrude","CAP_FACE",FACE,{"disambiguationData":[OSD([sQuery(id+"F15.wireOp",EDGE,"E129"),sQuery(id+"F15.wireOp",EDGE,"E130"),sQuery(id+"F15.wireOp",EDGE,"E131"),sQuery(id+"F15.wireOp",EDGE,"E132"),sQuery(id+"F15.wireOp",EDGE,"E133.MirrorCS"),sQuery(id+"F15.wireOp",EDGE,"E134.MirrorCS"),sQuery(id+"F15.wireOp",EDGE,"E135.MirrorCS"),sQuery(id+"F15.wireOp",EDGE,"E136.MirrorCS"),sQuery(id+"F15.wireOp",EDGE,"E146.MirrorCS"),sQuery(id+"F15.wireOp",EDGE,"E145")])],"isStart":true}),makeQuery(id+"F16.opExtrude","CAP_FACE",FACE,{"disambiguationData":[OSD([sQuery(id+"F15.wireOp",EDGE,"E137.MirrorCS"),sQuery(id+"F15.wireOp",EDGE,"E138.MirrorCS"),sQuery(id+"F15.wireOp",EDGE,"E139.MirrorCS"),sQuery(id+"F15.wireOp",EDGE,"E140.MirrorCS"),sQuery(id+"F15.wireOp",EDGE,"E141.MirrorCS"),sQuery(id+"F15.wireOp",EDGE,"E142.MirrorCS"),sQuery(id+"F15.wireOp",EDGE,"E143.MirrorCS"),sQuery(id+"F15.wireOp",EDGE,"E144.MirrorCS"),sQuery(id+"F15.wireOp",EDGE,"E147.MirrorCS"),sQuery(id+"F15.wireOp",EDGE,"E148.MirrorCS")])],"isStart":true})]});
            var sketch = newSketch(context, id + "F17", { "sketchPlane" : qUnion([Q0])});
            skLineSegment(sketch, "E149", {"start": v(0, 64.05) * mm, "end": v(0, -64.05) * mm, "construction": true});
            skLineSegment(sketch, "E150", {"start": v(-77.5, 0) * mm, "end": v(77.5, 0) * mm, "construction": true});
            skArc(sketch, "E151", {"start": v(-134.2, -150) * mm, "mid": v(-130.51, -130.51) * mm, "end": v(-150, -134.2) * mm});
            skLineSegment(sketch, "E152", {"start": v(-134.2, -150) * mm, "end": v(-150, -150) * mm});
            skLineSegment(sketch, "E153", {"start": v(-150, -150) * mm, "end": v(-150, -134.2) * mm});
            skLineSegment(sketch, "E154.MirrorCS", {"start": v(150, -150) * mm, "end": v(150, -134.2) * mm});
            skLineSegment(sketch, "E155.MirrorCS", {"start": v(134.2, -150) * mm, "end": v(150, -150) * mm});
            skArc(sketch, "E156.MirrorCS", {"start": v(134.2, -150) * mm, "mid": v(130.51, -130.51) * mm, "end": v(150, -134.2) * mm});
            skLineSegment(sketch, "E157.MirrorCS", {"start": v(134.2, 150) * mm, "end": v(150, 150) * mm});
            skArc(sketch, "E158.MirrorCS", {"start": v(-134.2, 150) * mm, "mid": v(-130.51, 130.51) * mm, "end": v(-150, 134.2) * mm});
            skArc(sketch, "E159.MirrorCS", {"start": v(134.2, 150) * mm, "mid": v(130.51, 130.51) * mm, "end": v(150, 134.2) * mm});
            skLineSegment(sketch, "E160.MirrorCS", {"start": v(150, 150) * mm, "end": v(150, 134.2) * mm});
            skLineSegment(sketch, "E161.MirrorCS", {"start": v(-134.2, 150) * mm, "end": v(-150, 150) * mm});
            skLineSegment(sketch, "E162.MirrorCS", {"start": v(-150, 150) * mm, "end": v(-150, 134.2) * mm});
            skLineSegment(sketch, "E163.bottom", {"start": v(-150, 113) * mm, "end": v(-140, 113) * mm});
            skLineSegment(sketch, "E163.top", {"start": v(-150, 107) * mm, "end": v(-140, 107) * mm});
            skLineSegment(sketch, "E163.left", {"start": v(-150, 113) * mm, "end": v(-150, 107) * mm});
            skLineSegment(sketch, "E163.right", {"start": v(-140, 113) * mm, "end": v(-140, 107) * mm});
            skLineSegment(sketch, "E164.bottom", {"start": v(-150, 53) * mm, "end": v(-140, 53) * mm});
            skLineSegment(sketch, "E164.top", {"start": v(-150, 47) * mm, "end": v(-140, 47) * mm});
            skLineSegment(sketch, "E164.left", {"start": v(-150, 53) * mm, "end": v(-150, 47) * mm});
            skLineSegment(sketch, "E164.right", {"start": v(-140, 53) * mm, "end": v(-140, 47) * mm});
            skLineSegment(sketch, "E165.MirrorCS", {"start": v(150, 53) * mm, "end": v(150, 47) * mm});
            skLineSegment(sketch, "E166.MirrorCS", {"start": v(150, 113) * mm, "end": v(150, 107) * mm});
            skLineSegment(sketch, "E167.MirrorCS", {"start": v(140, 53) * mm, "end": v(140, 47) * mm});
            skLineSegment(sketch, "E168.MirrorCS", {"start": v(140, 113) * mm, "end": v(140, 107) * mm});
            skLineSegment(sketch, "E169.MirrorCS", {"start": v(150, 107) * mm, "end": v(140, 107) * mm});
            skLineSegment(sketch, "E170.MirrorCS", {"start": v(150, 53) * mm, "end": v(140, 53) * mm});
            skLineSegment(sketch, "E171.MirrorCS", {"start": v(150, 47) * mm, "end": v(140, 47) * mm});
            skLineSegment(sketch, "E172.MirrorCS", {"start": v(150, 113) * mm, "end": v(140, 113) * mm});
            skLineSegment(sketch, "E173.MirrorCS", {"start": v(140, -113) * mm, "end": v(140, -107) * mm});
            skLineSegment(sketch, "E174.MirrorCS", {"start": v(-140, -53) * mm, "end": v(-140, -47) * mm});
            skLineSegment(sketch, "E175.MirrorCS", {"start": v(150, -113) * mm, "end": v(150, -107) * mm});
            skLineSegment(sketch, "E176.MirrorCS", {"start": v(140, -53) * mm, "end": v(140, -47) * mm});
            skLineSegment(sketch, "E177.MirrorCS", {"start": v(-150, -53) * mm, "end": v(-150, -47) * mm});
            skLineSegment(sketch, "E178.MirrorCS", {"start": v(-140, -113) * mm, "end": v(-140, -107) * mm});
            skLineSegment(sketch, "E179.MirrorCS", {"start": v(150, -53) * mm, "end": v(150, -47) * mm});
            skLineSegment(sketch, "E180.MirrorCS", {"start": v(-150, -113) * mm, "end": v(-150, -107) * mm});
            skLineSegment(sketch, "E181.MirrorCS", {"start": v(150, -47) * mm, "end": v(140, -47) * mm});
            skLineSegment(sketch, "E182.MirrorCS", {"start": v(150, -107) * mm, "end": v(140, -107) * mm});
            skLineSegment(sketch, "E183.MirrorCS", {"start": v(150, -53) * mm, "end": v(140, -53) * mm});
            skLineSegment(sketch, "E184.MirrorCS", {"start": v(-150, -113) * mm, "end": v(-140, -113) * mm});
            skLineSegment(sketch, "E185.MirrorCS", {"start": v(-150, -53) * mm, "end": v(-140, -53) * mm});
            skLineSegment(sketch, "E186.MirrorCS", {"start": v(-150, -107) * mm, "end": v(-140, -107) * mm});
            skLineSegment(sketch, "E187.MirrorCS", {"start": v(150, -113) * mm, "end": v(140, -113) * mm});
            skLineSegment(sketch, "E188.MirrorCS", {"start": v(-150, -47) * mm, "end": v(-140, -47) * mm});
            skLineSegment(sketch, "E189", {"start": v(-150, 110) * mm, "end": v(-135, 110) * mm, "construction": true});
            skLineSegment(sketch, "E190", {"start": v(-150, 50) * mm, "end": v(-135, 50) * mm, "construction": true});
            skLineSegment(sketch, "E191.MirrorCS", {"start": v(150, 110) * mm, "end": v(135, 110) * mm, "construction": true});
            skLineSegment(sketch, "E192.MirrorCS", {"start": v(150, 50) * mm, "end": v(135, 50) * mm, "construction": true});
            skLineSegment(sketch, "E193.MirrorCS", {"start": v(-150, -110) * mm, "end": v(-135, -110) * mm, "construction": true});
            skLineSegment(sketch, "E194.MirrorCS", {"start": v(-150, -50) * mm, "end": v(-135, -50) * mm, "construction": true});
            skLineSegment(sketch, "E195.MirrorCS", {"start": v(150, -110) * mm, "end": v(135, -110) * mm, "construction": true});
            skLineSegment(sketch, "E196.MirrorCS", {"start": v(150, -50) * mm, "end": v(135, -50) * mm, "construction": true});
            skSolve(sketch);
        }
        {
            var Q0;
            Q0=makeQuery(id+"F16.boolean.opBoolean","MERGE",FACE,{"derivedFrom":[makeQuery(id+"F1.opExtrude","CAP_FACE",FACE,{"disambiguationData":[OSD([sQuery(id+"F0.wireOp",EDGE,"E0.bottom"),sQuery(id+"F0.wireOp",EDGE,"E0.top"),sQuery(id+"F0.wireOp",EDGE,"E0.left"),sQuery(id+"F0.wireOp",EDGE,"E0.right"),sQuery(id+"F0.wireOp",EDGE,"E9"),sQuery(id+"F0.wireOp",EDGE,"E11"),sQuery(id+"F0.wireOp",EDGE,"E12"),sQuery(id+"F0.wireOp",EDGE,"E13"),sQuery(id+"F0.wireOp",EDGE,"E14"),sQuery(id+"F0.wireOp",EDGE,"E15"),sQuery(id+"F0.wireOp",EDGE,"E16.trimOffspring"),sQuery(id+"F0.wireOp",EDGE,"E18"),sQuery(id+"F0.wireOp",EDGE,"E19"),sQuery(id+"F0.wireOp",EDGE,"E20"),sQuery(id+"F0.wireOp",EDGE,"E21"),sQuery(id+"F0.wireOp",EDGE,"E22"),sQuery(id+"F0.wireOp",EDGE,"E23"),sQuery(id+"F0.wireOp",EDGE,"E24.trimOffspring"),sQuery(id+"F0.wireOp",EDGE,"E27.bottom"),sQuery(id+"F0.wireOp",EDGE,"E27.top"),sQuery(id+"F0.wireOp",EDGE,"E27.left"),sQuery(id+"F0.wireOp",EDGE,"E27.right"),sQuery(id+"F0.wireOp",EDGE,"E28"),sQuery(id+"F0.wireOp",EDGE,"E29"),sQuery(id+"F0.wireOp",EDGE,"E33.bottom"),sQuery(id+"F0.wireOp",EDGE,"E33.top"),sQuery(id+"F0.wireOp",EDGE,"E33.left"),sQuery(id+"F0.wireOp",EDGE,"E33.right"),sQuery(id+"F0.wireOp",EDGE,"E34"),sQuery(id+"F0.wireOp",EDGE,"E35"),sQuery(id+"F0.wireOp",EDGE,"E36.bottom"),sQuery(id+"F0.wireOp",EDGE,"E36.top"),sQuery(id+"F0.wireOp",EDGE,"E36.left"),sQuery(id+"F0.wireOp",EDGE,"E37"),sQuery(id+"F0.wireOp",EDGE,"E38"),sQuery(id+"F0.wireOp",EDGE,"E39"),sQuery(id+"F0.wireOp",EDGE,"E40"),sQuery(id+"F0.wireOp",EDGE,"E41"),sQuery(id+"F0.wireOp",EDGE,"E42"),sQuery(id+"F0.wireOp",EDGE,"E43")])],"isStart":false}),makeQuery(id+"F16.opExtrude","CAP_FACE",FACE,{"disambiguationData":[OSD([sQuery(id+"F15.wireOp",EDGE,"E129"),sQuery(id+"F15.wireOp",EDGE,"E130"),sQuery(id+"F15.wireOp",EDGE,"E131"),sQuery(id+"F15.wireOp",EDGE,"E132"),sQuery(id+"F15.wireOp",EDGE,"E133.MirrorCS"),sQuery(id+"F15.wireOp",EDGE,"E134.MirrorCS"),sQuery(id+"F15.wireOp",EDGE,"E135.MirrorCS"),sQuery(id+"F15.wireOp",EDGE,"E136.MirrorCS"),sQuery(id+"F15.wireOp",EDGE,"E146.MirrorCS"),sQuery(id+"F15.wireOp",EDGE,"E145")])],"isStart":true}),makeQuery(id+"F16.opExtrude","CAP_FACE",FACE,{"disambiguationData":[OSD([sQuery(id+"F15.wireOp",EDGE,"E137.MirrorCS"),sQuery(id+"F15.wireOp",EDGE,"E138.MirrorCS"),sQuery(id+"F15.wireOp",EDGE,"E139.MirrorCS"),sQuery(id+"F15.wireOp",EDGE,"E140.MirrorCS"),sQuery(id+"F15.wireOp",EDGE,"E141.MirrorCS"),sQuery(id+"F15.wireOp",EDGE,"E142.MirrorCS"),sQuery(id+"F15.wireOp",EDGE,"E143.MirrorCS"),sQuery(id+"F15.wireOp",EDGE,"E144.MirrorCS"),sQuery(id+"F15.wireOp",EDGE,"E147.MirrorCS"),sQuery(id+"F15.wireOp",EDGE,"E148.MirrorCS")])],"isStart":true})]});
            var sketch = newSketch(context, id + "F18", { "sketchPlane" : qUnion([Q0])});
            skLineSegment(sketch, "E197", {"start": v(135, -150) * mm, "end": v(135, -125) * mm, "construction": true});
            skLineSegment(sketch, "E198", {"start": v(120, -125) * mm, "end": v(150, -125) * mm, "construction": true});
            skPoint(sketch, "E199", {"position": v(145, -125) * mm});
            skPoint(sketch, "E200.MirrorP", {"position": v(125, -125) * mm});
            skPoint(sketch, "E201", {"position": v(125, -145) * mm});
            skLineSegment(sketch, "E202", {"start": v(125, -125) * mm, "end": v(125, -145) * mm, "construction": true});
            skLineSegment(sketch, "E203", {"start": v(0, 64.05) * mm, "end": v(0, -64.05) * mm, "construction": true});
            skLineSegment(sketch, "E204", {"start": v(-77.5, 0) * mm, "end": v(77.5, 0) * mm, "construction": true});
            skPoint(sketch, "E205.MirrorP", {"position": v(-145, -125) * mm});
            skPoint(sketch, "E206.MirrorP", {"position": v(-125, -125) * mm});
            skPoint(sketch, "E207.MirrorP", {"position": v(-125, -145) * mm});
            skLineSegment(sketch, "E208.MirrorCS", {"start": v(-120, -125) * mm, "end": v(-150, -125) * mm, "construction": true});
            skLineSegment(sketch, "E209.MirrorCS", {"start": v(-125, -125) * mm, "end": v(-125, -145) * mm, "construction": true});
            skLineSegment(sketch, "E210.MirrorCS", {"start": v(-135, -150) * mm, "end": v(-135, -125) * mm, "construction": true});
            skPoint(sketch, "E211.MirrorP", {"position": v(145, 125) * mm});
            skPoint(sketch, "E212.MirrorP", {"position": v(125, 145) * mm});
            skPoint(sketch, "E213.MirrorP", {"position": v(-125, 145) * mm});
            skPoint(sketch, "E214.MirrorP", {"position": v(-145, 125) * mm});
            skPoint(sketch, "E215.MirrorP", {"position": v(125, 125) * mm});
            skPoint(sketch, "E216.MirrorP", {"position": v(-125, 125) * mm});
            skSolve(sketch);
        }
        {
            var Q0;
            Q0 = qSketchRegion(id + "F17", true);
            extrude(context, id + "F19", {"entities" : qUnion([Q0]), "operationType" : NewBodyOperationType.REMOVE, "endBound" : BoundingType.THROUGH_ALL, "oppositeDirection" : true, "depth" : 25 * mm});
        }
        {
            var Q0;
            Q0=makeQuery(id+"F19.boolean.opBoolean","COPY",EDGE,{"derivedFrom":makeQuery(id+"F19.opExtrude","SWEPT_EDGE",EDGE,{"disambiguationData":[OSD([sQuery(id+"F15.wireOp",EDGE,"E143.MirrorCS"),sQuery(id+"F17.wireOp",EDGE,"E151"),sQuery(id+"F17.wireOp",EDGE,"E152")])]})});
            var Q1;
            Q1=makeQuery(id+"F19.boolean.opBoolean","COPY",EDGE,{"derivedFrom":makeQuery(id+"F19.opExtrude","SWEPT_EDGE",EDGE,{"disambiguationData":[OSD([sQuery(id+"F0.wireOp",EDGE,"E24.trimOffspring"),sQuery(id+"F15.wireOp",EDGE,"E137.MirrorCS"),sQuery(id+"F17.wireOp",EDGE,"E151"),sQuery(id+"F17.wireOp",EDGE,"E153")])]})});
            var Q2;
            Q2=makeQuery(id+"F16.opExtrude","SWEPT_EDGE",EDGE,{"disambiguationData":[OSD([sQuery(id+"F15.wireOp",EDGE,"E143.MirrorCS"),sQuery(id+"F15.wireOp",EDGE,"E144.MirrorCS")])]});
            var Q3;
            Q3=makeQuery(id+"F16.opExtrude","SWEPT_EDGE",EDGE,{"disambiguationData":[OSD([sQuery(id+"F15.wireOp",EDGE,"E139.MirrorCS"),sQuery(id+"F15.wireOp",EDGE,"E141.MirrorCS")])]});
            var Q4;
            Q4=makeQuery(id+"F19.boolean.opBoolean","COPY",EDGE,{"derivedFrom":makeQuery(id+"F19.opExtrude","SWEPT_EDGE",EDGE,{"disambiguationData":[OSD([sQuery(id+"F15.wireOp",EDGE,"E141.MirrorCS"),sQuery(id+"F17.wireOp",EDGE,"E156.MirrorCS"),sQuery(id+"F17.wireOp",EDGE,"E155.MirrorCS")])]})});
            var Q5;
            Q5=makeQuery(id+"F19.boolean.opBoolean","COPY",EDGE,{"derivedFrom":makeQuery(id+"F19.opExtrude","SWEPT_EDGE",EDGE,{"disambiguationData":[OSD([sQuery(id+"F0.wireOp",EDGE,"E16.trimOffspring"),sQuery(id+"F15.wireOp",EDGE,"E138.MirrorCS"),sQuery(id+"F17.wireOp",EDGE,"E154.MirrorCS"),sQuery(id+"F17.wireOp",EDGE,"E156.MirrorCS")])]})});
            var Q6;
            Q6=makeQuery(id+"F19.boolean.opBoolean","COPY",EDGE,{"derivedFrom":makeQuery(id+"F19.opExtrude","SWEPT_EDGE",EDGE,{"disambiguationData":[OSD([sQuery(id+"F0.wireOp",EDGE,"E0.left"),sQuery(id+"F15.wireOp",EDGE,"E133.MirrorCS"),sQuery(id+"F17.wireOp",EDGE,"E159.MirrorCS"),sQuery(id+"F17.wireOp",EDGE,"E160.MirrorCS")])]})});
            var Q7;
            Q7=makeQuery(id+"F19.boolean.opBoolean","COPY",EDGE,{"derivedFrom":makeQuery(id+"F19.opExtrude","SWEPT_EDGE",EDGE,{"disambiguationData":[OSD([sQuery(id+"F15.wireOp",EDGE,"E134.MirrorCS"),sQuery(id+"F17.wireOp",EDGE,"E159.MirrorCS"),sQuery(id+"F17.wireOp",EDGE,"E157.MirrorCS")])]})});
            var Q8;
            Q8=makeQuery(id+"F16.opExtrude","SWEPT_EDGE",EDGE,{"disambiguationData":[OSD([sQuery(id+"F15.wireOp",EDGE,"E134.MirrorCS"),sQuery(id+"F15.wireOp",EDGE,"E135.MirrorCS")])]});
            var Q9;
            Q9=makeQuery(id+"F16.opExtrude","SWEPT_EDGE",EDGE,{"disambiguationData":[OSD([sQuery(id+"F15.wireOp",EDGE,"E130"),sQuery(id+"F15.wireOp",EDGE,"E131")])]});
            var Q10;
            Q10=makeQuery(id+"F19.boolean.opBoolean","COPY",EDGE,{"derivedFrom":makeQuery(id+"F19.opExtrude","SWEPT_EDGE",EDGE,{"disambiguationData":[OSD([sQuery(id+"F15.wireOp",EDGE,"E130"),sQuery(id+"F17.wireOp",EDGE,"E158.MirrorCS"),sQuery(id+"F17.wireOp",EDGE,"E161.MirrorCS")])]})});
            var Q11;
            Q11=makeQuery(id+"F19.boolean.opBoolean","COPY",EDGE,{"derivedFrom":makeQuery(id+"F19.opExtrude","SWEPT_EDGE",EDGE,{"disambiguationData":[OSD([sQuery(id+"F0.wireOp",EDGE,"E0.right"),sQuery(id+"F15.wireOp",EDGE,"E129"),sQuery(id+"F17.wireOp",EDGE,"E158.MirrorCS"),sQuery(id+"F17.wireOp",EDGE,"E162.MirrorCS")])]})});
            fillet(context, id + "F20", {"entities" : qUnion([Q0, Q1, Q2, Q3, Q4, Q5, Q6, Q7, Q8, Q9, Q10, Q11]), "radius" : 3 * mm, "tangentPropagation" : true, "allowEdgeOverflow" : false});
        }
        {
            var Q0;
            Q0=sQuery(id+"F18.wireOp",VERTEX,"E214.MirrorP");
            var Q1;
            Q1=sQuery(id+"F18.wireOp",VERTEX,"E213.MirrorP");
            var Q2;
            Q2=sQuery(id+"F18.wireOp",VERTEX,"E216.MirrorP");
            var Q3;
            Q3=sQuery(id+"F18.wireOp",VERTEX,"E211.MirrorP");
            var Q4;
            Q4=sQuery(id+"F18.wireOp",VERTEX,"E215.MirrorP");
            var Q5;
            Q5=sQuery(id+"F18.wireOp",VERTEX,"E212.MirrorP");
            var Q6;
            Q6=sQuery(id+"F18.wireOp",VERTEX,"E205.MirrorP");
            var Q7;
            Q7=sQuery(id+"F18.wireOp",VERTEX,"E206.MirrorP");
            var Q8;
            Q8=sQuery(id+"F18.wireOp",VERTEX,"E207.MirrorP");
            var Q9;
            Q9=sQuery(id+"F18.wireOp",VERTEX,"E201");
            var Q10;
            Q10=sQuery(id+"F18.wireOp",VERTEX,"E199");
            var Q11;
            Q11=sQuery(id+"F18.wireOp",VERTEX,"E200.MirrorP");
            var Q12;
            Q12=sQuery(id+"F17.wireOp",VERTEX,"E189.end");
            var Q13;
            Q13=sQuery(id+"F17.wireOp",VERTEX,"E190.end");
            var Q14;
            Q14=sQuery(id+"F17.wireOp",VERTEX,"E194.MirrorCS.end");
            var Q15;
            Q15=sQuery(id+"F17.wireOp",VERTEX,"E193.MirrorCS.end");
            var Q16;
            Q16=sQuery(id+"F17.wireOp",VERTEX,"E195.MirrorCS.end");
            var Q17;
            Q17=sQuery(id+"F17.wireOp",VERTEX,"E196.MirrorCS.end");
            var Q18;
            Q18=sQuery(id+"F17.wireOp",VERTEX,"E192.MirrorCS.end");
            var Q19;
            Q19=sQuery(id+"F17.wireOp",VERTEX,"E191.MirrorCS.end");
            var Q20;
            Q20=makeQuery(id+"F1.opExtrude","SWEPT_BODY",BODY,{"disambiguationData":[OSD([sQuery(id+"F0.wireOp",EDGE,"E0.bottom"),sQuery(id+"F0.wireOp",EDGE,"E0.top"),sQuery(id+"F0.wireOp",EDGE,"E0.left"),sQuery(id+"F0.wireOp",EDGE,"E0.right"),sQuery(id+"F0.wireOp",EDGE,"E9"),sQuery(id+"F0.wireOp",EDGE,"E11"),sQuery(id+"F0.wireOp",EDGE,"E12"),sQuery(id+"F0.wireOp",EDGE,"E13"),sQuery(id+"F0.wireOp",EDGE,"E14"),sQuery(id+"F0.wireOp",EDGE,"E15"),sQuery(id+"F0.wireOp",EDGE,"E16.trimOffspring"),sQuery(id+"F0.wireOp",EDGE,"E18"),sQuery(id+"F0.wireOp",EDGE,"E19"),sQuery(id+"F0.wireOp",EDGE,"E20"),sQuery(id+"F0.wireOp",EDGE,"E21"),sQuery(id+"F0.wireOp",EDGE,"E22"),sQuery(id+"F0.wireOp",EDGE,"E23"),sQuery(id+"F0.wireOp",EDGE,"E24.trimOffspring"),sQuery(id+"F0.wireOp",EDGE,"E27.bottom"),sQuery(id+"F0.wireOp",EDGE,"E27.top"),sQuery(id+"F0.wireOp",EDGE,"E27.left"),sQuery(id+"F0.wireOp",EDGE,"E27.right"),sQuery(id+"F0.wireOp",EDGE,"E28"),sQuery(id+"F0.wireOp",EDGE,"E29"),sQuery(id+"F0.wireOp",EDGE,"E33.bottom"),sQuery(id+"F0.wireOp",EDGE,"E33.top"),sQuery(id+"F0.wireOp",EDGE,"E33.left"),sQuery(id+"F0.wireOp",EDGE,"E33.right"),sQuery(id+"F0.wireOp",EDGE,"E34"),sQuery(id+"F0.wireOp",EDGE,"E35"),sQuery(id+"F0.wireOp",EDGE,"E36.bottom"),sQuery(id+"F0.wireOp",EDGE,"E36.top"),sQuery(id+"F0.wireOp",EDGE,"E36.left"),sQuery(id+"F0.wireOp",EDGE,"E37"),sQuery(id+"F0.wireOp",EDGE,"E38"),sQuery(id+"F0.wireOp",EDGE,"E39"),sQuery(id+"F0.wireOp",EDGE,"E40"),sQuery(id+"F0.wireOp",EDGE,"E41"),sQuery(id+"F0.wireOp",EDGE,"E42"),sQuery(id+"F0.wireOp",EDGE,"E43")])]});
            hole(context, id + "F21", {"style" : HoleStyle.SIMPLE, "endStyle" : HoleEndStyle.THROUGH, "standardTappedOrClearance" : lookupTablePath({ "standard" : "ISO", "fit" : "Normal", "size" : "M3", "type" : "Clearance" }), "standardBlindInLast" : lookupTablePath({ "fit" : "Standard", "standard" : "ISO", "size" : "M3", "type" : "Clearance" }), "holeDiameter" : 3.3 * mm, "isTappedThrough" : true, "tappedDepth" : 12 * mm, "tapClearance" : 3, "locations" : qUnion([Q0, Q1, Q2, Q3, Q4, Q5, Q6, Q7, Q8, Q9, Q10, Q11, Q12, Q13, Q14, Q15, Q16, Q17, Q18, Q19]), "scope" : qUnion([Q20])});
        }
        {
            var Q0;
            Q0=makeQuery(id+"F19.boolean.opBoolean","COPY",FACE,{"derivedFrom":makeQuery(id+"F19.opExtrude","SWEPT_FACE",FACE,{"disambiguationData":[OSD([sQuery(id+"F17.wireOp",EDGE,"E163.bottom")])]})});
            var sketch = newSketch(context, id + "F22", { "sketchPlane" : qUnion([Q0])});
            skLineSegment(sketch, "E217", {"start": v(-150, 0) * mm, "end": v(-140, 0) * mm});
            skLineSegment(sketch, "E218", {"start": v(-140, 0) * mm, "end": v(-140, 6) * mm});
            skLineSegment(sketch, "E219", {"start": v(-130, 6) * mm, "end": v(-130, 294) * mm});
            skLineSegment(sketch, "E220", {"start": v(-140, 294) * mm, "end": v(-140, 300) * mm});
            skLineSegment(sketch, "E221", {"start": v(-140, 300) * mm, "end": v(-150, 300) * mm});
            skLineSegment(sketch, "E222", {"start": v(-150, 300) * mm, "end": v(-150, 290) * mm});
            skLineSegment(sketch, "E223", {"start": v(-150, 290) * mm, "end": v(-147, 290) * mm});
            skLineSegment(sketch, "E224", {"start": v(-147, 290) * mm, "end": v(-147, 10) * mm});
            skLineSegment(sketch, "E225", {"start": v(-147, 10) * mm, "end": v(-150, 10) * mm});
            skLineSegment(sketch, "E226", {"start": v(-150, 10) * mm, "end": v(-150, 0) * mm});
            skLineSegment(sketch, "E227", {"start": v(-140, 6) * mm, "end": v(-136.6, 6) * mm});
            skLineSegment(sketch, "E228", {"start": v(-136.6, 6) * mm, "end": v(-136.6, 9.75) * mm});
            skLineSegment(sketch, "E229", {"start": v(-136.6, 9.75) * mm, "end": v(-137.8, 9.75) * mm});
            skLineSegment(sketch, "E230", {"start": v(-137.8, 9.75) * mm, "end": v(-137.8, 12.25) * mm});
            skLineSegment(sketch, "E231", {"start": v(-137.8, 12.25) * mm, "end": v(-136.6, 12.25) * mm});
            skLineSegment(sketch, "E232", {"start": v(-136.6, 12.25) * mm, "end": v(-136.6, 16) * mm});
            skLineSegment(sketch, "E233", {"start": v(-136.6, 16) * mm, "end": v(-133.4, 16) * mm});
            skLineSegment(sketch, "E234", {"start": v(-133.4, 16) * mm, "end": v(-133.4, 12.25) * mm});
            skLineSegment(sketch, "E235", {"start": v(-133.4, 12.25) * mm, "end": v(-132.2, 12.25) * mm});
            skLineSegment(sketch, "E236", {"start": v(-132.2, 12.25) * mm, "end": v(-132.2, 9.75) * mm});
            skLineSegment(sketch, "E237", {"start": v(-132.2, 9.75) * mm, "end": v(-133.4, 9.75) * mm});
            skLineSegment(sketch, "E238", {"start": v(-133.4, 9.75) * mm, "end": v(-133.4, 6) * mm});
            skLineSegment(sketch, "E239", {"start": v(-133.4, 6) * mm, "end": v(-130, 6) * mm});
            skLineSegment(sketch, "E240", {"start": v(-130, 150) * mm, "end": v(-147, 150) * mm, "construction": true});
            skLineSegment(sketch, "E241.MirrorCS", {"start": v(-137.8, 290.25) * mm, "end": v(-137.8, 287.75) * mm});
            skLineSegment(sketch, "E242.MirrorCS", {"start": v(-132.2, 290.25) * mm, "end": v(-133.4, 290.25) * mm});
            skLineSegment(sketch, "E243.MirrorCS", {"start": v(-133.4, 290.25) * mm, "end": v(-133.4, 294) * mm});
            skLineSegment(sketch, "E244.MirrorCS", {"start": v(-132.2, 287.75) * mm, "end": v(-132.2, 290.25) * mm});
            skLineSegment(sketch, "E245.MirrorCS", {"start": v(-133.4, 284) * mm, "end": v(-133.4, 287.75) * mm});
            skLineSegment(sketch, "E246.MirrorCS", {"start": v(-137.8, 287.75) * mm, "end": v(-136.6, 287.75) * mm});
            skLineSegment(sketch, "E247.MirrorCS", {"start": v(-140, 294) * mm, "end": v(-136.6, 294) * mm});
            skLineSegment(sketch, "E248.MirrorCS", {"start": v(-133.4, 287.75) * mm, "end": v(-132.2, 287.75) * mm});
            skLineSegment(sketch, "E249.MirrorCS", {"start": v(-136.6, 287.75) * mm, "end": v(-136.6, 284) * mm});
            skLineSegment(sketch, "E250.MirrorCS", {"start": v(-136.6, 294) * mm, "end": v(-136.6, 290.25) * mm});
            skLineSegment(sketch, "E251.MirrorCS", {"start": v(-133.4, 294) * mm, "end": v(-130, 294) * mm});
            skLineSegment(sketch, "E252.MirrorCS", {"start": v(-136.6, 284) * mm, "end": v(-133.4, 284) * mm});
            skLineSegment(sketch, "E253.MirrorCS", {"start": v(-136.6, 290.25) * mm, "end": v(-137.8, 290.25) * mm});
            skSolve(sketch);
        }
        {
            var Q0;
            Q0 = qSketchRegion(id + "F22", true);
            extrude(context, id + "F23", {"entities" : qUnion([Q0]), "depth" : 6 * mm, "offsetDistance" : 25 * mm});
        }
        {
            var Q0;
            {var subQ9=sQuery(id+"F15.wireOp",EDGE,"E129");var subQ46=sQuery(id+"F0.wireOp",EDGE,"E0.right");Q0=makeQuery(id+"F19.boolean.opBoolean","SPLIT",FACE,{"disambiguationData":[TD([makeQuery(id+"F19.opExtrude","SWEPT_FACE",FACE,{"disambiguationData":[OSD([sQuery(id+"F17.wireOp",EDGE,"E158.MirrorCS")])]})])],"derivedFrom":makeQuery(id+"F16.boolean.opBoolean","MERGE",FACE,{"derivedFrom":[makeQuery(id+"F1.opExtrude","SWEPT_FACE",FACE,{"disambiguationData":[OSD([subQ46])]}),makeQuery(id+"F16.opExtrude","SWEPT_FACE",FACE,{"disambiguationData":[OSD([subQ9])]})]})});}
            var sketch = newSketch(context, id + "F24", { "sketchPlane" : qUnion([Q0])});
            skLineSegment(sketch, "E254", {"start": v(-140, 29) * mm, "end": v(-113, 29) * mm});
            skLineSegment(sketch, "E255", {"start": v(-113, 29) * mm, "end": v(-113, 10) * mm});
            skLineSegment(sketch, "E256", {"start": v(-113, 10) * mm, "end": v(-107, 10) * mm});
            skLineSegment(sketch, "E257", {"start": v(-107, 10) * mm, "end": v(-107, 6) * mm});
            skLineSegment(sketch, "E258", {"start": v(-107, 6) * mm, "end": v(-53, 6) * mm});
            skLineSegment(sketch, "E259", {"start": v(-53, 6) * mm, "end": v(-53, 10) * mm});
            skLineSegment(sketch, "E260", {"start": v(-53, 10) * mm, "end": v(-47, 10) * mm});
            skLineSegment(sketch, "E261", {"start": v(-47, 10) * mm, "end": v(-47, 6) * mm});
            skLineSegment(sketch, "E262", {"start": v(-47, 6) * mm, "end": v(47, 6) * mm});
            skLineSegment(sketch, "E263", {"start": v(47, 6) * mm, "end": v(47, 10) * mm});
            skLineSegment(sketch, "E264", {"start": v(47, 10) * mm, "end": v(53, 10) * mm});
            skLineSegment(sketch, "E265", {"start": v(53, 10) * mm, "end": v(53, 6) * mm});
            skLineSegment(sketch, "E266", {"start": v(53, 6) * mm, "end": v(107, 6) * mm});
            skLineSegment(sketch, "E267", {"start": v(107, 6) * mm, "end": v(107, 10) * mm});
            skLineSegment(sketch, "E268", {"start": v(107, 10) * mm, "end": v(113, 10) * mm});
            skLineSegment(sketch, "E269", {"start": v(113, 10) * mm, "end": v(113, 29) * mm});
            skLineSegment(sketch, "E270", {"start": v(113, 29) * mm, "end": v(140, 29) * mm});
            skLineSegment(sketch, "E271", {"start": v(-140, 150) * mm, "end": v(140, 150) * mm, "construction": true});
            skLineSegment(sketch, "E272", {"start": v(-140, 29) * mm, "end": v(-140, 150) * mm});
            skLineSegment(sketch, "E273", {"start": v(140, 29) * mm, "end": v(140, 150) * mm});
            skLineSegment(sketch, "E274.MirrorCS", {"start": v(-53, 290) * mm, "end": v(-47, 290) * mm});
            skLineSegment(sketch, "E275.MirrorCS", {"start": v(-53, 294) * mm, "end": v(-53, 290) * mm});
            skLineSegment(sketch, "E276.MirrorCS", {"start": v(-113, 290) * mm, "end": v(-107, 290) * mm});
            skLineSegment(sketch, "E277.MirrorCS", {"start": v(53, 290) * mm, "end": v(53, 294) * mm});
            skLineSegment(sketch, "E278.MirrorCS", {"start": v(47, 290) * mm, "end": v(53, 290) * mm});
            skLineSegment(sketch, "E279.MirrorCS", {"start": v(47, 294) * mm, "end": v(47, 290) * mm});
            skLineSegment(sketch, "E280.MirrorCS", {"start": v(-107, 290) * mm, "end": v(-107, 294) * mm});
            skLineSegment(sketch, "E281.MirrorCS", {"start": v(-47, 290) * mm, "end": v(-47, 294) * mm});
            skLineSegment(sketch, "E282.MirrorCS", {"start": v(107, 290) * mm, "end": v(113, 290) * mm});
            skLineSegment(sketch, "E283.MirrorCS", {"start": v(107, 294) * mm, "end": v(107, 290) * mm});
            skLineSegment(sketch, "E284.MirrorCS", {"start": v(-107, 294) * mm, "end": v(-53, 294) * mm});
            skLineSegment(sketch, "E285.MirrorCS", {"start": v(53, 294) * mm, "end": v(107, 294) * mm});
            skLineSegment(sketch, "E286.MirrorCS", {"start": v(-47, 294) * mm, "end": v(47, 294) * mm});
            skLineSegment(sketch, "E287", {"start": v(-113, 290) * mm, "end": v(-113, 294) * mm});
            skLineSegment(sketch, "E288", {"start": v(-113, 294) * mm, "end": v(-140, 294) * mm});
            skLineSegment(sketch, "E289", {"start": v(-140, 294) * mm, "end": v(-140, 150) * mm});
            skLineSegment(sketch, "E290", {"start": v(113, 290) * mm, "end": v(113, 294) * mm});
            skLineSegment(sketch, "E291", {"start": v(113, 294) * mm, "end": v(140, 294) * mm});
            skLineSegment(sketch, "E292", {"start": v(140, 294) * mm, "end": v(140, 150) * mm});
            skSolve(sketch);
        }
        {
            var Q0;
            Q0 = qSketchRegion(id + "F24", true);
            extrude(context, id + "F25", {"entities" : qUnion([Q0]), "depth" : 3 * mm, "offsetDistance" : 25 * mm});
        }
        {
            var Q0;
            Q0=makeQuery(id+"F23.opExtrude","SWEPT_FACE",FACE,{"disambiguationData":[OSD([sQuery(id+"F22.wireOp",EDGE,"E221")])]});
            var sketch = newSketch(context, id + "F26", { "sketchPlane" : qUnion([Q0])});
            skLineSegment(sketch, "E293", {"start": v(-150, 140) * mm, "end": v(-150, 113) * mm});
            skLineSegment(sketch, "E294", {"start": v(-150, 113) * mm, "end": v(-140, 113) * mm});
            skLineSegment(sketch, "E295", {"start": v(-140, 113) * mm, "end": v(-140, 107) * mm});
            skLineSegment(sketch, "E296", {"start": v(-140, 107) * mm, "end": v(-150, 107) * mm});
            skLineSegment(sketch, "E297", {"start": v(-150, 107) * mm, "end": v(-150, 53) * mm});
            skLineSegment(sketch, "E298", {"start": v(-150, 53) * mm, "end": v(-140, 53) * mm});
            skLineSegment(sketch, "E299", {"start": v(-140, 53) * mm, "end": v(-140, 47) * mm});
            skLineSegment(sketch, "E300", {"start": v(-140, 47) * mm, "end": v(-150, 47) * mm});
            skLineSegment(sketch, "E301", {"start": v(-77.5, 0) * mm, "end": v(77.5, 0) * mm, "construction": true});
            skLineSegment(sketch, "E302", {"start": v(0, 64.05) * mm, "end": v(0, -64.05) * mm, "construction": true});
            skLineSegment(sketch, "E303", {"start": v(-150, 47) * mm, "end": v(-150, 0) * mm});
            skLineSegment(sketch, "E304", {"start": v(-150, 140) * mm, "end": v(0, 140) * mm});
            skLineSegment(sketch, "E305.MirrorCS", {"start": v(-140, -53) * mm, "end": v(-140, -47) * mm});
            skLineSegment(sketch, "E306.MirrorCS", {"start": v(-140, -113) * mm, "end": v(-140, -107) * mm});
            skLineSegment(sketch, "E307.MirrorCS", {"start": v(-140, -47) * mm, "end": v(-150, -47) * mm});
            skLineSegment(sketch, "E308.MirrorCS", {"start": v(-150, -53) * mm, "end": v(-140, -53) * mm});
            skLineSegment(sketch, "E309.MirrorCS", {"start": v(-150, -140) * mm, "end": v(0, -140) * mm});
            skLineSegment(sketch, "E310.MirrorCS", {"start": v(-140, -107) * mm, "end": v(-150, -107) * mm});
            skLineSegment(sketch, "E311.MirrorCS", {"start": v(-150, -107) * mm, "end": v(-150, -53) * mm});
            skLineSegment(sketch, "E312.MirrorCS", {"start": v(-150, -47) * mm, "end": v(-150, 0) * mm});
            skLineSegment(sketch, "E313.MirrorCS", {"start": v(-150, -113) * mm, "end": v(-140, -113) * mm});
            skLineSegment(sketch, "E314.MirrorCS", {"start": v(-150, -140) * mm, "end": v(-150, -113) * mm});
            skLineSegment(sketch, "E315.MirrorCS", {"start": v(140, 47) * mm, "end": v(150, 47) * mm});
            skLineSegment(sketch, "E316.MirrorCS", {"start": v(140, -53) * mm, "end": v(140, -47) * mm});
            skLineSegment(sketch, "E317.MirrorCS", {"start": v(140, 113) * mm, "end": v(140, 107) * mm});
            skLineSegment(sketch, "E318.MirrorCS", {"start": v(150, 113) * mm, "end": v(140, 113) * mm});
            skLineSegment(sketch, "E319.MirrorCS", {"start": v(140, 107) * mm, "end": v(150, 107) * mm});
            skLineSegment(sketch, "E320.MirrorCS", {"start": v(140, 53) * mm, "end": v(140, 47) * mm});
            skLineSegment(sketch, "E321.MirrorCS", {"start": v(150, 53) * mm, "end": v(140, 53) * mm});
            skLineSegment(sketch, "E322.MirrorCS", {"start": v(140, -107) * mm, "end": v(150, -107) * mm});
            skLineSegment(sketch, "E323.MirrorCS", {"start": v(140, -113) * mm, "end": v(140, -107) * mm});
            skLineSegment(sketch, "E324.MirrorCS", {"start": v(150, -113) * mm, "end": v(140, -113) * mm});
            skLineSegment(sketch, "E325.MirrorCS", {"start": v(140, -47) * mm, "end": v(150, -47) * mm});
            skLineSegment(sketch, "E326.MirrorCS", {"start": v(150, -53) * mm, "end": v(140, -53) * mm});
            skLineSegment(sketch, "E327.MirrorCS", {"start": v(150, 140) * mm, "end": v(0, 140) * mm});
            skLineSegment(sketch, "E328.MirrorCS", {"start": v(150, 47) * mm, "end": v(150, 0) * mm});
            skLineSegment(sketch, "E329.MirrorCS", {"start": v(150, 140) * mm, "end": v(150, 113) * mm});
            skLineSegment(sketch, "E330.MirrorCS", {"start": v(150, 107) * mm, "end": v(150, 53) * mm});
            skLineSegment(sketch, "E331.MirrorCS", {"start": v(150, -140) * mm, "end": v(150, -113) * mm});
            skLineSegment(sketch, "E332.MirrorCS", {"start": v(150, -140) * mm, "end": v(0, -140) * mm});
            skLineSegment(sketch, "E333.MirrorCS", {"start": v(150, -47) * mm, "end": v(150, 0) * mm});
            skLineSegment(sketch, "E334.MirrorCS", {"start": v(150, -107) * mm, "end": v(150, -53) * mm});
            skLineSegment(sketch, "E335.bottom", {"start": v(120, 64.05) * mm, "end": v(-120, 64.05) * mm});
            skLineSegment(sketch, "E335.top", {"start": v(120, 120) * mm, "end": v(-120, 120) * mm});
            skLineSegment(sketch, "E335.left", {"start": v(120, 64.05) * mm, "end": v(120, 120) * mm});
            skLineSegment(sketch, "E335.right", {"start": v(-120, 64.05) * mm, "end": v(-120, 120) * mm});
            skPoint(sketch, "E335.middle", {"position": v(0, 92.02) * mm});
            skLineSegment(sketch, "E336.MirrorCS", {"start": v(-120, -64.05) * mm, "end": v(-120, -120) * mm});
            skLineSegment(sketch, "E337.MirrorCS", {"start": v(120, -120) * mm, "end": v(-120, -120) * mm});
            skLineSegment(sketch, "E338.MirrorCS", {"start": v(120, -64.05) * mm, "end": v(120, -120) * mm});
            skLineSegment(sketch, "E339.MirrorCS", {"start": v(120, -64.05) * mm, "end": v(-120, -64.05) * mm});
            skSolve(sketch);
        }
        {
            var Q0;
            Q0 = qSketchRegion(id + "F26", true);
            extrude(context, id + "F27", {"entities" : qUnion([Q0]), "depth" : 6 * mm, "offsetDistance" : 25 * mm});
        }
        {
            var Q0;
            Q0=makeQuery(id+"F27.opExtrude","SWEPT_EDGE",EDGE,{"disambiguationData":[OSD([sQuery(id+"F26.wireOp",EDGE,"E335.top"),sQuery(id+"F26.wireOp",EDGE,"E335.right")])]});
            var Q1;
            Q1=makeQuery(id+"F27.opExtrude","SWEPT_EDGE",EDGE,{"disambiguationData":[OSD([sQuery(id+"F26.wireOp",EDGE,"E335.bottom"),sQuery(id+"F26.wireOp",EDGE,"E335.right")])]});
            var Q2;
            Q2=makeQuery(id+"F27.opExtrude","SWEPT_EDGE",EDGE,{"disambiguationData":[OSD([sQuery(id+"F26.wireOp",EDGE,"E335.top"),sQuery(id+"F26.wireOp",EDGE,"E335.left")])]});
            var Q3;
            Q3=makeQuery(id+"F27.opExtrude","SWEPT_EDGE",EDGE,{"disambiguationData":[OSD([sQuery(id+"F26.wireOp",EDGE,"E335.bottom"),sQuery(id+"F26.wireOp",EDGE,"E335.left")])]});
            var Q4;
            Q4=makeQuery(id+"F27.opExtrude","SWEPT_EDGE",EDGE,{"disambiguationData":[OSD([sQuery(id+"F26.wireOp",EDGE,"E337.MirrorCS"),sQuery(id+"F26.wireOp",EDGE,"E338.MirrorCS")])]});
            var Q5;
            Q5=makeQuery(id+"F27.opExtrude","SWEPT_EDGE",EDGE,{"disambiguationData":[OSD([sQuery(id+"F26.wireOp",EDGE,"E338.MirrorCS"),sQuery(id+"F26.wireOp",EDGE,"E339.MirrorCS")])]});
            var Q6;
            Q6=makeQuery(id+"F27.opExtrude","SWEPT_EDGE",EDGE,{"disambiguationData":[OSD([sQuery(id+"F26.wireOp",EDGE,"E336.MirrorCS"),sQuery(id+"F26.wireOp",EDGE,"E339.MirrorCS")])]});
            var Q7;
            Q7=makeQuery(id+"F27.opExtrude","SWEPT_EDGE",EDGE,{"disambiguationData":[OSD([sQuery(id+"F26.wireOp",EDGE,"E336.MirrorCS"),sQuery(id+"F26.wireOp",EDGE,"E337.MirrorCS")])]});
            fillet(context, id + "F28", {"entities" : qUnion([Q0, Q1, Q2, Q3, Q4, Q5, Q6, Q7]), "radius" : 5 * mm, "tangentPropagation" : true, "allowEdgeOverflow" : false});
        }
    });
